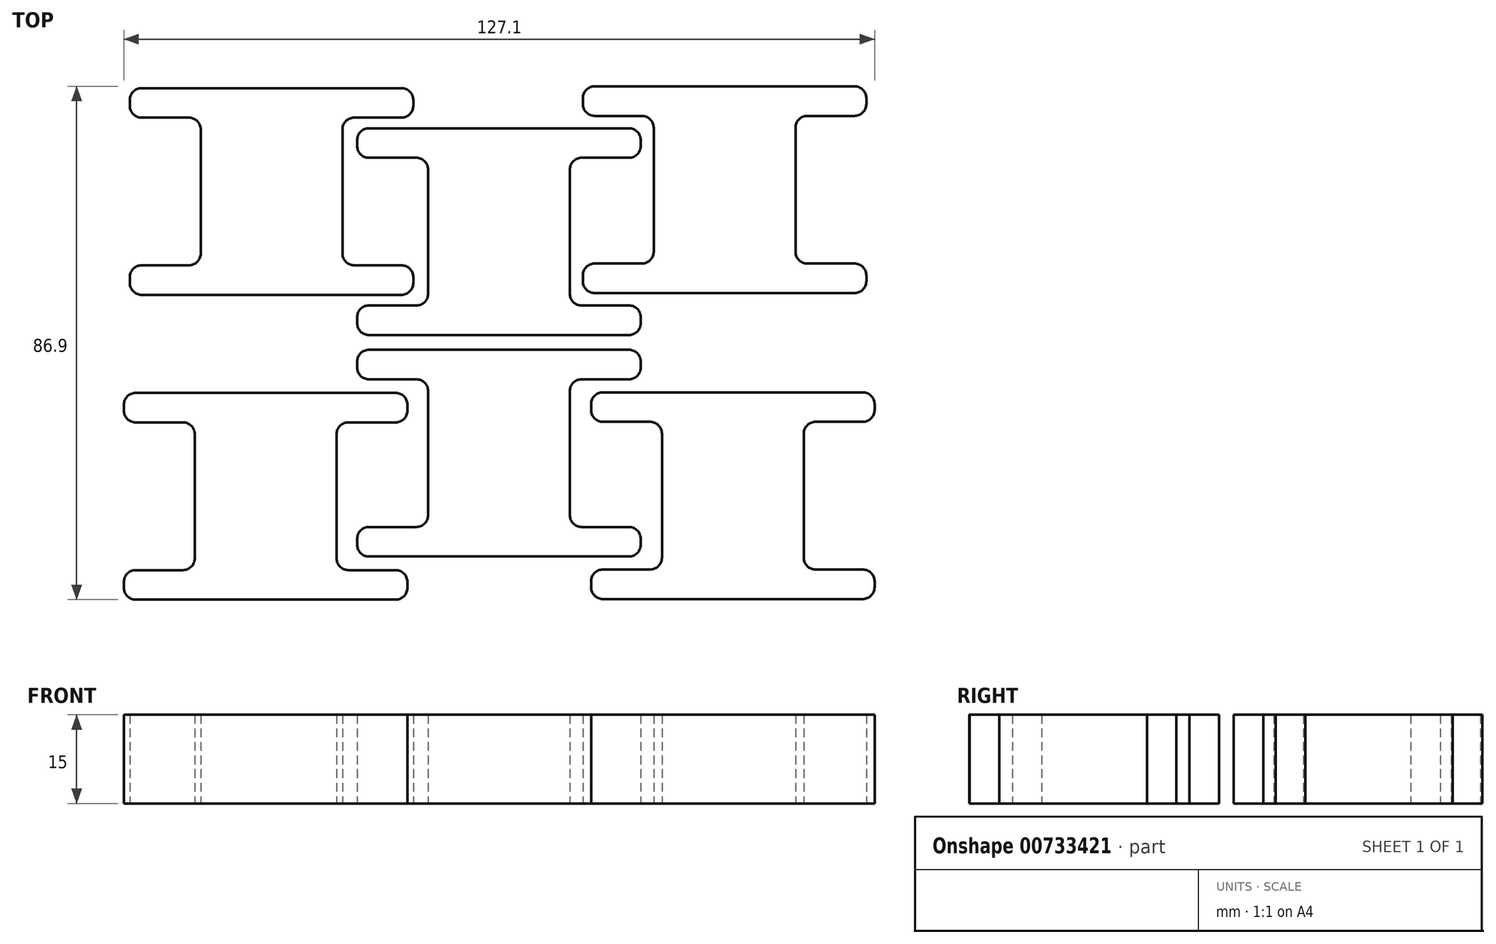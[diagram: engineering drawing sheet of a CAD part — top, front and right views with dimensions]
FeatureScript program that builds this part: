
annotation { "Feature Type Name" : "Feature", "Feature Type Description" : "" }
export const myFeature = defineFeature(function(context is Context, id is Id, definition is map)
    precondition{}
    {
        {
            var Q0;
            Q0=qCreatedBy(makeId("Top.planeOp"),FACE);
            var sketch = newSketch(context, id + "F0", { "sketchPlane" : qUnion([Q0])});
            skLineSegment(sketch, "E0", {"start": v(-10, -2.53) * mm, "end": v(-2, -2.53) * mm});
            skLineSegment(sketch, "E1", {"start": v(0, -4.53) * mm, "end": v(0, -25.53) * mm});
            skLineSegment(sketch, "E2", {"start": v(-2, -27.53) * mm, "end": v(-10, -27.53) * mm});
            skLineSegment(sketch, "E3", {"start": v(-12, -0.53) * mm, "end": v(-12, 0.47) * mm});
            skLineSegment(sketch, "E4", {"start": v(-10, 2.47) * mm, "end": v(12, 2.47) * mm});
            skLineSegment(sketch, "E5", {"start": v(12, 2.47) * mm, "end": v(12, -32.53) * mm});
            skLineSegment(sketch, "E6", {"start": v(12, -32.53) * mm, "end": v(-10, -32.53) * mm});
            skLineSegment(sketch, "E7", {"start": v(-12, -30.53) * mm, "end": v(-12, -29.53) * mm});
            skPoint(sketch, "E8.visualSharp", {"position": v(0, -2.53) * mm});
            skArc(sketch, "E8.filletArc", {"start": v(0, -4.53) * mm, "mid": v(-0.59, -3.12) * mm, "end": v(-2, -2.53) * mm});
            skPoint(sketch, "E9.visualSharp", {"position": v(0, -27.53) * mm});
            skArc(sketch, "E9.filletArc", {"start": v(-2, -27.53) * mm, "mid": v(-0.59, -26.94) * mm, "end": v(0, -25.53) * mm});
            skPoint(sketch, "E10.visualSharp", {"position": v(-12, -27.53) * mm});
            skArc(sketch, "E10.filletArc", {"start": v(-10, -27.53) * mm, "mid": v(-11.41, -28.12) * mm, "end": v(-12, -29.53) * mm});
            skPoint(sketch, "E11.visualSharp", {"position": v(-12, -32.53) * mm});
            skArc(sketch, "E11.filletArc", {"start": v(-12, -30.53) * mm, "mid": v(-11.41, -31.94) * mm, "end": v(-10, -32.53) * mm});
            skPoint(sketch, "E12.visualSharp", {"position": v(-12, -2.53) * mm});
            skArc(sketch, "E12.filletArc", {"start": v(-12, -0.53) * mm, "mid": v(-11.41, -1.94) * mm, "end": v(-10, -2.53) * mm});
            skPoint(sketch, "E13.visualSharp", {"position": v(-12, 2.47) * mm});
            skArc(sketch, "E13.filletArc", {"start": v(-10, 2.47) * mm, "mid": v(-11.41, 1.88) * mm, "end": v(-12, 0.47) * mm});
            skLineSegment(sketch, "E14.MirrorCS", {"start": v(36, -0.53) * mm, "end": v(36, 0.47) * mm});
            skLineSegment(sketch, "E15.MirrorCS", {"start": v(36, -30.53) * mm, "end": v(36, -29.53) * mm});
            skArc(sketch, "E16.MirrorCS", {"start": v(36, -0.53) * mm, "mid": v(35.41, -1.94) * mm, "end": v(34, -2.53) * mm});
            skArc(sketch, "E17.MirrorCS", {"start": v(26, -27.53) * mm, "mid": v(24.59, -26.94) * mm, "end": v(24, -25.53) * mm});
            skArc(sketch, "E18.MirrorCS", {"start": v(36, -30.53) * mm, "mid": v(35.41, -31.94) * mm, "end": v(34, -32.53) * mm});
            skArc(sketch, "E19.MirrorCS", {"start": v(34, -27.53) * mm, "mid": v(35.41, -28.12) * mm, "end": v(36, -29.53) * mm});
            skArc(sketch, "E20.MirrorCS", {"start": v(34, 2.47) * mm, "mid": v(35.41, 1.88) * mm, "end": v(36, 0.47) * mm});
            skArc(sketch, "E21.MirrorCS", {"start": v(24, -4.53) * mm, "mid": v(24.59, -3.12) * mm, "end": v(26, -2.53) * mm});
            skPoint(sketch, "E22.MirrorP", {"position": v(24, -27.53) * mm});
            skLineSegment(sketch, "E23.MirrorCS", {"start": v(34, -2.53) * mm, "end": v(26, -2.53) * mm});
            skPoint(sketch, "E24.MirrorP", {"position": v(24, -2.53) * mm});
            skLineSegment(sketch, "E25.MirrorCS", {"start": v(26, -27.53) * mm, "end": v(34, -27.53) * mm});
            skLineSegment(sketch, "E26.MirrorCS", {"start": v(34, 2.47) * mm, "end": v(12, 2.47) * mm});
            skPoint(sketch, "E27.MirrorP", {"position": v(36, -32.53) * mm});
            skLineSegment(sketch, "E28.MirrorCS", {"start": v(12, -32.53) * mm, "end": v(34, -32.53) * mm});
            skLineSegment(sketch, "E29.MirrorCS", {"start": v(24, -4.53) * mm, "end": v(24, -25.53) * mm});
            skPoint(sketch, "E30.MirrorP", {"position": v(36, 2.47) * mm});
            skPoint(sketch, "E31.MirrorP", {"position": v(36, -2.53) * mm});
            skPoint(sketch, "E32.MirrorP", {"position": v(36, -27.53) * mm});
            skSolve(sketch);
        }
        {
            var Q0;
            Q0=makeQuery(id+"F0.imprint","IMPRINT",FACE,{"disambiguationData":[TD([[makeQuery(id+"F0.imprint","IMPRINT",EDGE,{"derivedFrom":sQuery(id+"F0.wireOp",EDGE,"E0")}),1.0]])]});
            var Q1;
            Q1=makeQuery(id+"F0.imprint","IMPRINT",FACE,{"disambiguationData":[TD([[makeQuery(id+"F0.imprint","IMPRINT",EDGE,{"derivedFrom":sQuery(id+"F0.wireOp",EDGE,"E5")}),1.0]])]});
            extrude(context, id + "F1", {"entities" : qUnion([Q0, Q1]), "depth" : 15 * mm, "offsetDistance" : 25 * mm});
        }
        {
            var Q0;
            Q0=makeQuery(id+"F1.opExtrude","SWEPT_BODY",BODY,{"disambiguationData":[OSD([sQuery(id+"F0.wireOp",EDGE,"E0"),sQuery(id+"F0.wireOp",EDGE,"E1"),sQuery(id+"F0.wireOp",EDGE,"E2"),sQuery(id+"F0.wireOp",EDGE,"E3"),sQuery(id+"F0.wireOp",EDGE,"E4"),sQuery(id+"F0.wireOp",EDGE,"E6"),sQuery(id+"F0.wireOp",EDGE,"E7"),sQuery(id+"F0.wireOp",EDGE,"E8.filletArc"),sQuery(id+"F0.wireOp",EDGE,"E9.filletArc"),sQuery(id+"F0.wireOp",EDGE,"E10.filletArc"),sQuery(id+"F0.wireOp",EDGE,"E11.filletArc"),sQuery(id+"F0.wireOp",EDGE,"E12.filletArc"),sQuery(id+"F0.wireOp",EDGE,"E13.filletArc"),sQuery(id+"F0.wireOp",EDGE,"E14.MirrorCS"),sQuery(id+"F0.wireOp",EDGE,"E15.MirrorCS"),sQuery(id+"F0.wireOp",EDGE,"E16.MirrorCS"),sQuery(id+"F0.wireOp",EDGE,"E17.MirrorCS"),sQuery(id+"F0.wireOp",EDGE,"E18.MirrorCS"),sQuery(id+"F0.wireOp",EDGE,"E19.MirrorCS"),sQuery(id+"F0.wireOp",EDGE,"E20.MirrorCS"),sQuery(id+"F0.wireOp",EDGE,"E21.MirrorCS"),sQuery(id+"F0.wireOp",EDGE,"E23.MirrorCS"),sQuery(id+"F0.wireOp",EDGE,"E25.MirrorCS"),sQuery(id+"F0.wireOp",EDGE,"E26.MirrorCS"),sQuery(id+"F0.wireOp",EDGE,"E28.MirrorCS"),sQuery(id+"F0.wireOp",EDGE,"E29.MirrorCS")])]});
            transform(context, id + "F2", {"entities" : qUnion([Q0]), "transformType" : TransformType.TRANSLATION_3D, "dx" : 39.6 * mm, "dy" : -7.2 * mm, "dz" : 0 * mm, "makeCopy" : true});
        }
        {
            var Q0;
            Q0=makeQuery(id+"F1.opExtrude","SWEPT_BODY",BODY,{"disambiguationData":[OSD([sQuery(id+"F0.wireOp",EDGE,"E0"),sQuery(id+"F0.wireOp",EDGE,"E1"),sQuery(id+"F0.wireOp",EDGE,"E2"),sQuery(id+"F0.wireOp",EDGE,"E3"),sQuery(id+"F0.wireOp",EDGE,"E4"),sQuery(id+"F0.wireOp",EDGE,"E6"),sQuery(id+"F0.wireOp",EDGE,"E7"),sQuery(id+"F0.wireOp",EDGE,"E8.filletArc"),sQuery(id+"F0.wireOp",EDGE,"E9.filletArc"),sQuery(id+"F0.wireOp",EDGE,"E10.filletArc"),sQuery(id+"F0.wireOp",EDGE,"E11.filletArc"),sQuery(id+"F0.wireOp",EDGE,"E12.filletArc"),sQuery(id+"F0.wireOp",EDGE,"E13.filletArc"),sQuery(id+"F0.wireOp",EDGE,"E14.MirrorCS"),sQuery(id+"F0.wireOp",EDGE,"E15.MirrorCS"),sQuery(id+"F0.wireOp",EDGE,"E16.MirrorCS"),sQuery(id+"F0.wireOp",EDGE,"E17.MirrorCS"),sQuery(id+"F0.wireOp",EDGE,"E18.MirrorCS"),sQuery(id+"F0.wireOp",EDGE,"E19.MirrorCS"),sQuery(id+"F0.wireOp",EDGE,"E20.MirrorCS"),sQuery(id+"F0.wireOp",EDGE,"E21.MirrorCS"),sQuery(id+"F0.wireOp",EDGE,"E23.MirrorCS"),sQuery(id+"F0.wireOp",EDGE,"E25.MirrorCS"),sQuery(id+"F0.wireOp",EDGE,"E26.MirrorCS"),sQuery(id+"F0.wireOp",EDGE,"E28.MirrorCS"),sQuery(id+"F0.wireOp",EDGE,"E29.MirrorCS")])]});
            transform(context, id + "F3", {"entities" : qUnion([Q0]), "transformType" : TransformType.TRANSLATION_3D, "dx" : -39.5 * mm, "dy" : -7.3 * mm, "dz" : 0 * mm, "makeCopy" : true});
        }
        {
            var Q0;
            Q0=makeQuery(id+"F1.opExtrude","SWEPT_BODY",BODY,{"disambiguationData":[OSD([sQuery(id+"F0.wireOp",EDGE,"E0"),sQuery(id+"F0.wireOp",EDGE,"E1"),sQuery(id+"F0.wireOp",EDGE,"E2"),sQuery(id+"F0.wireOp",EDGE,"E3"),sQuery(id+"F0.wireOp",EDGE,"E4"),sQuery(id+"F0.wireOp",EDGE,"E6"),sQuery(id+"F0.wireOp",EDGE,"E7"),sQuery(id+"F0.wireOp",EDGE,"E8.filletArc"),sQuery(id+"F0.wireOp",EDGE,"E9.filletArc"),sQuery(id+"F0.wireOp",EDGE,"E10.filletArc"),sQuery(id+"F0.wireOp",EDGE,"E11.filletArc"),sQuery(id+"F0.wireOp",EDGE,"E12.filletArc"),sQuery(id+"F0.wireOp",EDGE,"E13.filletArc"),sQuery(id+"F0.wireOp",EDGE,"E14.MirrorCS"),sQuery(id+"F0.wireOp",EDGE,"E15.MirrorCS"),sQuery(id+"F0.wireOp",EDGE,"E16.MirrorCS"),sQuery(id+"F0.wireOp",EDGE,"E17.MirrorCS"),sQuery(id+"F0.wireOp",EDGE,"E18.MirrorCS"),sQuery(id+"F0.wireOp",EDGE,"E19.MirrorCS"),sQuery(id+"F0.wireOp",EDGE,"E20.MirrorCS"),sQuery(id+"F0.wireOp",EDGE,"E21.MirrorCS"),sQuery(id+"F0.wireOp",EDGE,"E23.MirrorCS"),sQuery(id+"F0.wireOp",EDGE,"E25.MirrorCS"),sQuery(id+"F0.wireOp",EDGE,"E26.MirrorCS"),sQuery(id+"F0.wireOp",EDGE,"E28.MirrorCS"),sQuery(id+"F0.wireOp",EDGE,"E29.MirrorCS")])]});
            transform(context, id + "F4", {"entities" : qUnion([Q0]), "transformType" : TransformType.TRANSLATION_3D, "dx" : 0 * mm, "dy" : 37.5 * mm, "dz" : 0 * mm, "makeCopy" : true});
        }
        {
            var Q0;
            Q0=makeQuery(id+"F4.opPattern","COPY",BODY,{"derivedFrom":makeQuery(id+"F1.opExtrude","SWEPT_BODY",BODY,{"disambiguationData":[OSD([sQuery(id+"F0.wireOp",EDGE,"E0"),sQuery(id+"F0.wireOp",EDGE,"E1"),sQuery(id+"F0.wireOp",EDGE,"E2"),sQuery(id+"F0.wireOp",EDGE,"E3"),sQuery(id+"F0.wireOp",EDGE,"E4"),sQuery(id+"F0.wireOp",EDGE,"E6"),sQuery(id+"F0.wireOp",EDGE,"E7"),sQuery(id+"F0.wireOp",EDGE,"E8.filletArc"),sQuery(id+"F0.wireOp",EDGE,"E9.filletArc"),sQuery(id+"F0.wireOp",EDGE,"E10.filletArc"),sQuery(id+"F0.wireOp",EDGE,"E11.filletArc"),sQuery(id+"F0.wireOp",EDGE,"E12.filletArc"),sQuery(id+"F0.wireOp",EDGE,"E13.filletArc"),sQuery(id+"F0.wireOp",EDGE,"E14.MirrorCS"),sQuery(id+"F0.wireOp",EDGE,"E15.MirrorCS"),sQuery(id+"F0.wireOp",EDGE,"E16.MirrorCS"),sQuery(id+"F0.wireOp",EDGE,"E17.MirrorCS"),sQuery(id+"F0.wireOp",EDGE,"E18.MirrorCS"),sQuery(id+"F0.wireOp",EDGE,"E19.MirrorCS"),sQuery(id+"F0.wireOp",EDGE,"E20.MirrorCS"),sQuery(id+"F0.wireOp",EDGE,"E21.MirrorCS"),sQuery(id+"F0.wireOp",EDGE,"E23.MirrorCS"),sQuery(id+"F0.wireOp",EDGE,"E25.MirrorCS"),sQuery(id+"F0.wireOp",EDGE,"E26.MirrorCS"),sQuery(id+"F0.wireOp",EDGE,"E28.MirrorCS"),sQuery(id+"F0.wireOp",EDGE,"E29.MirrorCS")])]}),"instanceName":"1"});
            transform(context, id + "F5", {"entities" : qUnion([Q0]), "transformType" : TransformType.TRANSLATION_3D, "dx" : 38.2 * mm, "dy" : 7.1 * mm, "dz" : 0 * mm, "makeCopy" : true});
        }
        {
            var Q0;
            Q0=makeQuery(id+"F4.opPattern","COPY",BODY,{"derivedFrom":makeQuery(id+"F1.opExtrude","SWEPT_BODY",BODY,{"disambiguationData":[OSD([sQuery(id+"F0.wireOp",EDGE,"E0"),sQuery(id+"F0.wireOp",EDGE,"E1"),sQuery(id+"F0.wireOp",EDGE,"E2"),sQuery(id+"F0.wireOp",EDGE,"E3"),sQuery(id+"F0.wireOp",EDGE,"E4"),sQuery(id+"F0.wireOp",EDGE,"E6"),sQuery(id+"F0.wireOp",EDGE,"E7"),sQuery(id+"F0.wireOp",EDGE,"E8.filletArc"),sQuery(id+"F0.wireOp",EDGE,"E9.filletArc"),sQuery(id+"F0.wireOp",EDGE,"E10.filletArc"),sQuery(id+"F0.wireOp",EDGE,"E11.filletArc"),sQuery(id+"F0.wireOp",EDGE,"E12.filletArc"),sQuery(id+"F0.wireOp",EDGE,"E13.filletArc"),sQuery(id+"F0.wireOp",EDGE,"E14.MirrorCS"),sQuery(id+"F0.wireOp",EDGE,"E15.MirrorCS"),sQuery(id+"F0.wireOp",EDGE,"E16.MirrorCS"),sQuery(id+"F0.wireOp",EDGE,"E17.MirrorCS"),sQuery(id+"F0.wireOp",EDGE,"E18.MirrorCS"),sQuery(id+"F0.wireOp",EDGE,"E19.MirrorCS"),sQuery(id+"F0.wireOp",EDGE,"E20.MirrorCS"),sQuery(id+"F0.wireOp",EDGE,"E21.MirrorCS"),sQuery(id+"F0.wireOp",EDGE,"E23.MirrorCS"),sQuery(id+"F0.wireOp",EDGE,"E25.MirrorCS"),sQuery(id+"F0.wireOp",EDGE,"E26.MirrorCS"),sQuery(id+"F0.wireOp",EDGE,"E28.MirrorCS"),sQuery(id+"F0.wireOp",EDGE,"E29.MirrorCS")])]}),"instanceName":"1"});
            transform(context, id + "F6", {"entities" : qUnion([Q0]), "transformType" : TransformType.TRANSLATION_3D, "dx" : -38.5 * mm, "dy" : 6.8 * mm, "dz" : 0 * mm, "makeCopy" : true});
        }
        {
            var Q0;
            Q0=makeQuery(id+"F6.opPattern","COPY",BODY,{"derivedFrom":makeQuery(id+"F4.opPattern","COPY",BODY,{"derivedFrom":makeQuery(id+"F1.opExtrude","SWEPT_BODY",BODY,{"disambiguationData":[OSD([sQuery(id+"F0.wireOp",EDGE,"E0"),sQuery(id+"F0.wireOp",EDGE,"E1"),sQuery(id+"F0.wireOp",EDGE,"E2"),sQuery(id+"F0.wireOp",EDGE,"E3"),sQuery(id+"F0.wireOp",EDGE,"E4"),sQuery(id+"F0.wireOp",EDGE,"E6"),sQuery(id+"F0.wireOp",EDGE,"E7"),sQuery(id+"F0.wireOp",EDGE,"E8.filletArc"),sQuery(id+"F0.wireOp",EDGE,"E9.filletArc"),sQuery(id+"F0.wireOp",EDGE,"E10.filletArc"),sQuery(id+"F0.wireOp",EDGE,"E11.filletArc"),sQuery(id+"F0.wireOp",EDGE,"E12.filletArc"),sQuery(id+"F0.wireOp",EDGE,"E13.filletArc"),sQuery(id+"F0.wireOp",EDGE,"E14.MirrorCS"),sQuery(id+"F0.wireOp",EDGE,"E15.MirrorCS"),sQuery(id+"F0.wireOp",EDGE,"E16.MirrorCS"),sQuery(id+"F0.wireOp",EDGE,"E17.MirrorCS"),sQuery(id+"F0.wireOp",EDGE,"E18.MirrorCS"),sQuery(id+"F0.wireOp",EDGE,"E19.MirrorCS"),sQuery(id+"F0.wireOp",EDGE,"E20.MirrorCS"),sQuery(id+"F0.wireOp",EDGE,"E21.MirrorCS"),sQuery(id+"F0.wireOp",EDGE,"E23.MirrorCS"),sQuery(id+"F0.wireOp",EDGE,"E25.MirrorCS"),sQuery(id+"F0.wireOp",EDGE,"E26.MirrorCS"),sQuery(id+"F0.wireOp",EDGE,"E28.MirrorCS"),sQuery(id+"F0.wireOp",EDGE,"E29.MirrorCS")])]}),"instanceName":"1"}),"instanceName":"1"});
            transform(context, id + "F7", {"entities" : qUnion([Q0]), "transformType" : TransformType.TRANSLATION_3D, "dx" : 0 * mm, "dy" : 38.3 * mm, "dz" : 0 * mm, "makeCopy" : true});
        }
        {
            var Q0;
            Q0=makeQuery(id+"F4.opPattern","COPY",BODY,{"derivedFrom":makeQuery(id+"F1.opExtrude","SWEPT_BODY",BODY,{"disambiguationData":[OSD([sQuery(id+"F0.wireOp",EDGE,"E0"),sQuery(id+"F0.wireOp",EDGE,"E1"),sQuery(id+"F0.wireOp",EDGE,"E2"),sQuery(id+"F0.wireOp",EDGE,"E3"),sQuery(id+"F0.wireOp",EDGE,"E4"),sQuery(id+"F0.wireOp",EDGE,"E6"),sQuery(id+"F0.wireOp",EDGE,"E7"),sQuery(id+"F0.wireOp",EDGE,"E8.filletArc"),sQuery(id+"F0.wireOp",EDGE,"E9.filletArc"),sQuery(id+"F0.wireOp",EDGE,"E10.filletArc"),sQuery(id+"F0.wireOp",EDGE,"E11.filletArc"),sQuery(id+"F0.wireOp",EDGE,"E12.filletArc"),sQuery(id+"F0.wireOp",EDGE,"E13.filletArc"),sQuery(id+"F0.wireOp",EDGE,"E14.MirrorCS"),sQuery(id+"F0.wireOp",EDGE,"E15.MirrorCS"),sQuery(id+"F0.wireOp",EDGE,"E16.MirrorCS"),sQuery(id+"F0.wireOp",EDGE,"E17.MirrorCS"),sQuery(id+"F0.wireOp",EDGE,"E18.MirrorCS"),sQuery(id+"F0.wireOp",EDGE,"E19.MirrorCS"),sQuery(id+"F0.wireOp",EDGE,"E20.MirrorCS"),sQuery(id+"F0.wireOp",EDGE,"E21.MirrorCS"),sQuery(id+"F0.wireOp",EDGE,"E23.MirrorCS"),sQuery(id+"F0.wireOp",EDGE,"E25.MirrorCS"),sQuery(id+"F0.wireOp",EDGE,"E26.MirrorCS"),sQuery(id+"F0.wireOp",EDGE,"E28.MirrorCS"),sQuery(id+"F0.wireOp",EDGE,"E29.MirrorCS")])]}),"instanceName":"1"});
            transform(context, id + "F8", {"entities" : qUnion([Q0]), "transformType" : TransformType.TRANSLATION_3D, "dx" : 0 * mm, "dy" : 52.6 * mm, "dz" : 0 * mm, "makeCopy" : true});
        }
        {
            var Q0;
            Q0=makeQuery(id+"F5.opPattern","COPY",BODY,{"derivedFrom":makeQuery(id+"F4.opPattern","COPY",BODY,{"derivedFrom":makeQuery(id+"F1.opExtrude","SWEPT_BODY",BODY,{"disambiguationData":[OSD([sQuery(id+"F0.wireOp",EDGE,"E0"),sQuery(id+"F0.wireOp",EDGE,"E1"),sQuery(id+"F0.wireOp",EDGE,"E2"),sQuery(id+"F0.wireOp",EDGE,"E3"),sQuery(id+"F0.wireOp",EDGE,"E4"),sQuery(id+"F0.wireOp",EDGE,"E6"),sQuery(id+"F0.wireOp",EDGE,"E7"),sQuery(id+"F0.wireOp",EDGE,"E8.filletArc"),sQuery(id+"F0.wireOp",EDGE,"E9.filletArc"),sQuery(id+"F0.wireOp",EDGE,"E10.filletArc"),sQuery(id+"F0.wireOp",EDGE,"E11.filletArc"),sQuery(id+"F0.wireOp",EDGE,"E12.filletArc"),sQuery(id+"F0.wireOp",EDGE,"E13.filletArc"),sQuery(id+"F0.wireOp",EDGE,"E14.MirrorCS"),sQuery(id+"F0.wireOp",EDGE,"E15.MirrorCS"),sQuery(id+"F0.wireOp",EDGE,"E16.MirrorCS"),sQuery(id+"F0.wireOp",EDGE,"E17.MirrorCS"),sQuery(id+"F0.wireOp",EDGE,"E18.MirrorCS"),sQuery(id+"F0.wireOp",EDGE,"E19.MirrorCS"),sQuery(id+"F0.wireOp",EDGE,"E20.MirrorCS"),sQuery(id+"F0.wireOp",EDGE,"E21.MirrorCS"),sQuery(id+"F0.wireOp",EDGE,"E23.MirrorCS"),sQuery(id+"F0.wireOp",EDGE,"E25.MirrorCS"),sQuery(id+"F0.wireOp",EDGE,"E26.MirrorCS"),sQuery(id+"F0.wireOp",EDGE,"E28.MirrorCS"),sQuery(id+"F0.wireOp",EDGE,"E29.MirrorCS")])]}),"instanceName":"1"}),"instanceName":"1"});
            transform(context, id + "F9", {"entities" : qUnion([Q0]), "transformType" : TransformType.TRANSLATION_3D, "dx" : 0 * mm, "dy" : 38.5 * mm, "dz" : 0 * mm, "makeCopy" : true});
        }
        {
            var Q0;
            Q0=makeQuery(id+"F9.opPattern","COPY",BODY,{"derivedFrom":makeQuery(id+"F5.opPattern","COPY",BODY,{"derivedFrom":makeQuery(id+"F4.opPattern","COPY",BODY,{"derivedFrom":makeQuery(id+"F1.opExtrude","SWEPT_BODY",BODY,{"disambiguationData":[OSD([sQuery(id+"F0.wireOp",EDGE,"E0"),sQuery(id+"F0.wireOp",EDGE,"E1"),sQuery(id+"F0.wireOp",EDGE,"E2"),sQuery(id+"F0.wireOp",EDGE,"E3"),sQuery(id+"F0.wireOp",EDGE,"E4"),sQuery(id+"F0.wireOp",EDGE,"E6"),sQuery(id+"F0.wireOp",EDGE,"E7"),sQuery(id+"F0.wireOp",EDGE,"E8.filletArc"),sQuery(id+"F0.wireOp",EDGE,"E9.filletArc"),sQuery(id+"F0.wireOp",EDGE,"E10.filletArc"),sQuery(id+"F0.wireOp",EDGE,"E11.filletArc"),sQuery(id+"F0.wireOp",EDGE,"E12.filletArc"),sQuery(id+"F0.wireOp",EDGE,"E13.filletArc"),sQuery(id+"F0.wireOp",EDGE,"E14.MirrorCS"),sQuery(id+"F0.wireOp",EDGE,"E15.MirrorCS"),sQuery(id+"F0.wireOp",EDGE,"E16.MirrorCS"),sQuery(id+"F0.wireOp",EDGE,"E17.MirrorCS"),sQuery(id+"F0.wireOp",EDGE,"E18.MirrorCS"),sQuery(id+"F0.wireOp",EDGE,"E19.MirrorCS"),sQuery(id+"F0.wireOp",EDGE,"E20.MirrorCS"),sQuery(id+"F0.wireOp",EDGE,"E21.MirrorCS"),sQuery(id+"F0.wireOp",EDGE,"E23.MirrorCS"),sQuery(id+"F0.wireOp",EDGE,"E25.MirrorCS"),sQuery(id+"F0.wireOp",EDGE,"E26.MirrorCS"),sQuery(id+"F0.wireOp",EDGE,"E28.MirrorCS"),sQuery(id+"F0.wireOp",EDGE,"E29.MirrorCS")])]}),"instanceName":"1"}),"instanceName":"1"}),"instanceName":"1"});
            deleteBodies(context, id + "F10", {"entities" : qUnion([Q0])});
        }
        {
            var Q0;
            Q0=makeQuery(id+"F8.opPattern","COPY",BODY,{"derivedFrom":makeQuery(id+"F4.opPattern","COPY",BODY,{"derivedFrom":makeQuery(id+"F1.opExtrude","SWEPT_BODY",BODY,{"disambiguationData":[OSD([sQuery(id+"F0.wireOp",EDGE,"E0"),sQuery(id+"F0.wireOp",EDGE,"E1"),sQuery(id+"F0.wireOp",EDGE,"E2"),sQuery(id+"F0.wireOp",EDGE,"E3"),sQuery(id+"F0.wireOp",EDGE,"E4"),sQuery(id+"F0.wireOp",EDGE,"E6"),sQuery(id+"F0.wireOp",EDGE,"E7"),sQuery(id+"F0.wireOp",EDGE,"E8.filletArc"),sQuery(id+"F0.wireOp",EDGE,"E9.filletArc"),sQuery(id+"F0.wireOp",EDGE,"E10.filletArc"),sQuery(id+"F0.wireOp",EDGE,"E11.filletArc"),sQuery(id+"F0.wireOp",EDGE,"E12.filletArc"),sQuery(id+"F0.wireOp",EDGE,"E13.filletArc"),sQuery(id+"F0.wireOp",EDGE,"E14.MirrorCS"),sQuery(id+"F0.wireOp",EDGE,"E15.MirrorCS"),sQuery(id+"F0.wireOp",EDGE,"E16.MirrorCS"),sQuery(id+"F0.wireOp",EDGE,"E17.MirrorCS"),sQuery(id+"F0.wireOp",EDGE,"E18.MirrorCS"),sQuery(id+"F0.wireOp",EDGE,"E19.MirrorCS"),sQuery(id+"F0.wireOp",EDGE,"E20.MirrorCS"),sQuery(id+"F0.wireOp",EDGE,"E21.MirrorCS"),sQuery(id+"F0.wireOp",EDGE,"E23.MirrorCS"),sQuery(id+"F0.wireOp",EDGE,"E25.MirrorCS"),sQuery(id+"F0.wireOp",EDGE,"E26.MirrorCS"),sQuery(id+"F0.wireOp",EDGE,"E28.MirrorCS"),sQuery(id+"F0.wireOp",EDGE,"E29.MirrorCS")])]}),"instanceName":"1"}),"instanceName":"1"});
            deleteBodies(context, id + "F11", {"entities" : qUnion([Q0])});
        }
        {
            var Q0;
            Q0=makeQuery(id+"F7.opPattern","COPY",BODY,{"derivedFrom":makeQuery(id+"F6.opPattern","COPY",BODY,{"derivedFrom":makeQuery(id+"F4.opPattern","COPY",BODY,{"derivedFrom":makeQuery(id+"F1.opExtrude","SWEPT_BODY",BODY,{"disambiguationData":[OSD([sQuery(id+"F0.wireOp",EDGE,"E0"),sQuery(id+"F0.wireOp",EDGE,"E1"),sQuery(id+"F0.wireOp",EDGE,"E2"),sQuery(id+"F0.wireOp",EDGE,"E3"),sQuery(id+"F0.wireOp",EDGE,"E4"),sQuery(id+"F0.wireOp",EDGE,"E6"),sQuery(id+"F0.wireOp",EDGE,"E7"),sQuery(id+"F0.wireOp",EDGE,"E8.filletArc"),sQuery(id+"F0.wireOp",EDGE,"E9.filletArc"),sQuery(id+"F0.wireOp",EDGE,"E10.filletArc"),sQuery(id+"F0.wireOp",EDGE,"E11.filletArc"),sQuery(id+"F0.wireOp",EDGE,"E12.filletArc"),sQuery(id+"F0.wireOp",EDGE,"E13.filletArc"),sQuery(id+"F0.wireOp",EDGE,"E14.MirrorCS"),sQuery(id+"F0.wireOp",EDGE,"E15.MirrorCS"),sQuery(id+"F0.wireOp",EDGE,"E16.MirrorCS"),sQuery(id+"F0.wireOp",EDGE,"E17.MirrorCS"),sQuery(id+"F0.wireOp",EDGE,"E18.MirrorCS"),sQuery(id+"F0.wireOp",EDGE,"E19.MirrorCS"),sQuery(id+"F0.wireOp",EDGE,"E20.MirrorCS"),sQuery(id+"F0.wireOp",EDGE,"E21.MirrorCS"),sQuery(id+"F0.wireOp",EDGE,"E23.MirrorCS"),sQuery(id+"F0.wireOp",EDGE,"E25.MirrorCS"),sQuery(id+"F0.wireOp",EDGE,"E26.MirrorCS"),sQuery(id+"F0.wireOp",EDGE,"E28.MirrorCS"),sQuery(id+"F0.wireOp",EDGE,"E29.MirrorCS")])]}),"instanceName":"1"}),"instanceName":"1"}),"instanceName":"1"});
            deleteBodies(context, id + "F12", {"entities" : qUnion([Q0])});
        }
    });
